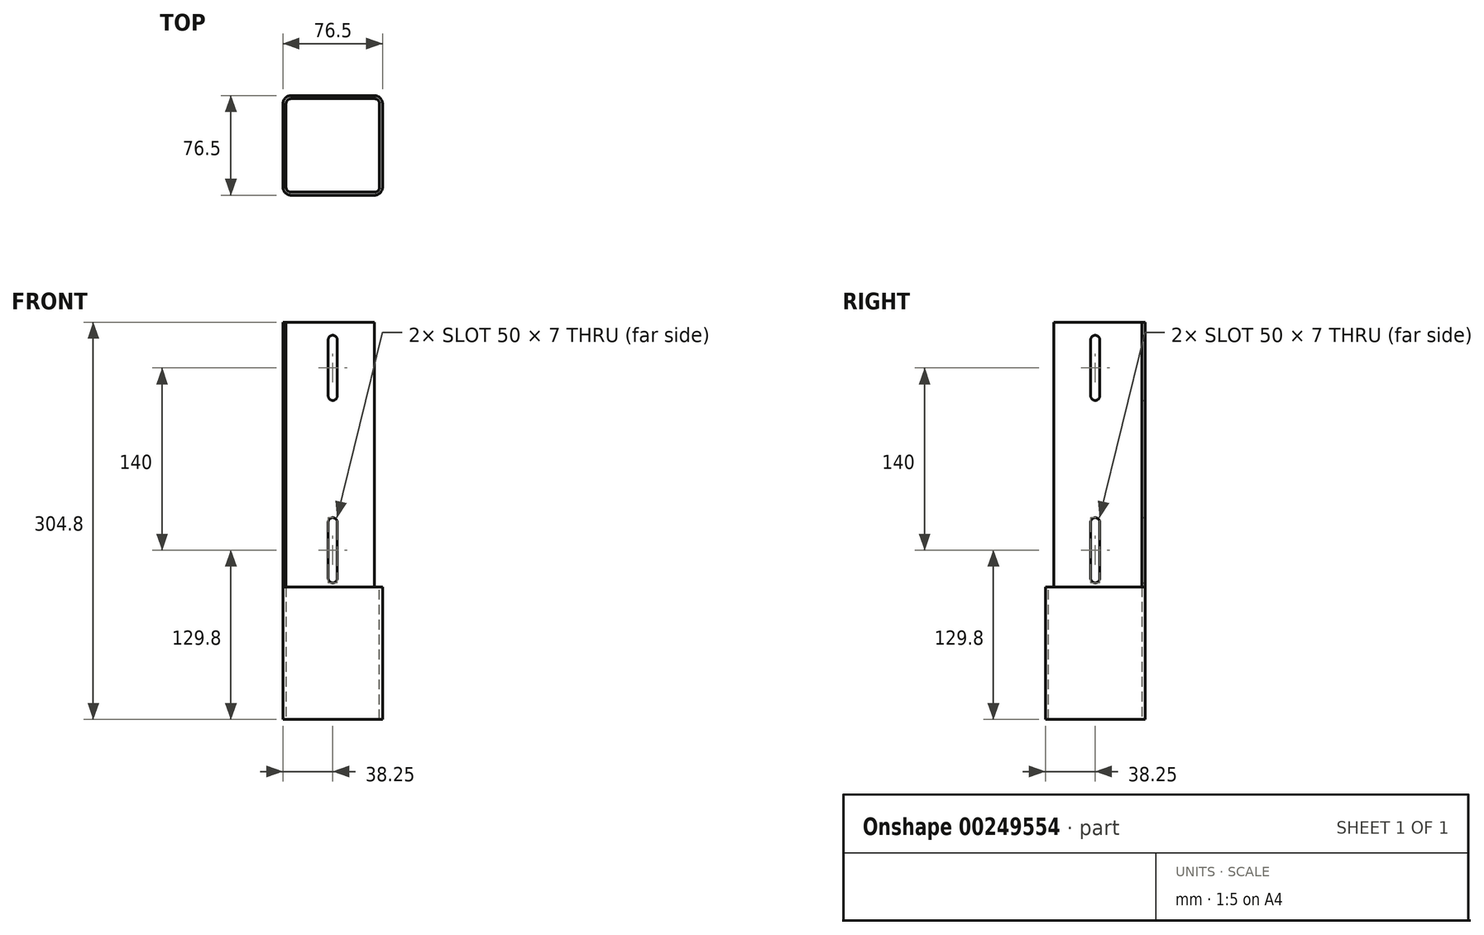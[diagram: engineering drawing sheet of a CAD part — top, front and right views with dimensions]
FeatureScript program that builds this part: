
annotation { "Feature Type Name" : "Feature", "Feature Type Description" : "" }
export const myFeature = defineFeature(function(context is Context, id is Id, definition is map)
    precondition{}
    {
        {
            var Q0;
            Q0=qCreatedBy(makeId("Top.planeOp"),FACE);
            var sketch = newSketch(context, id + "F0", { "sketchPlane" : qUnion([Q0])});
            skLineSegment(sketch, "E0.bottom", {"start": v(31.9, -38.25) * mm, "end": v(-31.9, -38.25) * mm});
            skLineSegment(sketch, "E0.top", {"start": v(31.9, 38.25) * mm, "end": v(-31.9, 38.25) * mm});
            skLineSegment(sketch, "E0.left", {"start": v(38.25, -31.9) * mm, "end": v(38.25, 31.9) * mm});
            skLineSegment(sketch, "E0.right", {"start": v(-38.25, -31.9) * mm, "end": v(-38.25, 31.9) * mm});
            skPoint(sketch, "E0.middle", {"position": v(0, 0) * mm});
            skPoint(sketch, "E1.visualSharp", {"position": v(-38.25, 38.25) * mm});
            skArc(sketch, "E1.filletArc", {"start": v(-31.9, 38.25) * mm, "mid": v(-36.39, 36.39) * mm, "end": v(-38.25, 31.9) * mm});
            skPoint(sketch, "E2.visualSharp", {"position": v(38.25, 38.25) * mm});
            skArc(sketch, "E2.filletArc", {"start": v(38.25, 31.9) * mm, "mid": v(36.39, 36.39) * mm, "end": v(31.9, 38.25) * mm});
            skPoint(sketch, "E3.visualSharp", {"position": v(38.25, -38.25) * mm});
            skArc(sketch, "E3.filletArc", {"start": v(31.9, -38.25) * mm, "mid": v(36.39, -36.39) * mm, "end": v(38.25, -31.9) * mm});
            skPoint(sketch, "E4.visualSharp", {"position": v(-38.25, -38.25) * mm});
            skArc(sketch, "E4.filletArc", {"start": v(-38.25, -31.9) * mm, "mid": v(-36.39, -36.39) * mm, "end": v(-31.9, -38.25) * mm});
            skSolve(sketch);
        }
        {
            var Q0;
            Q0 = qSketchRegion(id + "F0", true);
            extrude(context, id + "F1", {"entities" : qUnion([Q0]), "depth" : 304.8 * mm});
        }
        {
            var Q0;
            Q0=makeQuery(id+"F1.opExtrude","CAP_FACE",FACE,{"disambiguationData":[OSD([sQuery(id+"F0.wireOp",EDGE,"E0.bottom"),sQuery(id+"F0.wireOp",EDGE,"E0.top"),sQuery(id+"F0.wireOp",EDGE,"E0.left"),sQuery(id+"F0.wireOp",EDGE,"E0.right"),sQuery(id+"F0.wireOp",EDGE,"E1.filletArc"),sQuery(id+"F0.wireOp",EDGE,"E2.filletArc"),sQuery(id+"F0.wireOp",EDGE,"E3.filletArc"),sQuery(id+"F0.wireOp",EDGE,"E4.filletArc")])],"isStart":false});
            var Q1;
            Q1=makeQuery(id+"F1.opExtrude","CAP_FACE",FACE,{"disambiguationData":[OSD([sQuery(id+"F0.wireOp",EDGE,"E0.bottom"),sQuery(id+"F0.wireOp",EDGE,"E0.top"),sQuery(id+"F0.wireOp",EDGE,"E0.left"),sQuery(id+"F0.wireOp",EDGE,"E0.right"),sQuery(id+"F0.wireOp",EDGE,"E1.filletArc"),sQuery(id+"F0.wireOp",EDGE,"E2.filletArc"),sQuery(id+"F0.wireOp",EDGE,"E3.filletArc"),sQuery(id+"F0.wireOp",EDGE,"E4.filletArc")])],"isStart":true});
            shell(context, id + "F2", {"entities" : qUnion([Q0, Q1]), "thickness" : 2.36 * mm});
        }
        {
            var Q0;
            Q0=makeQuery(id+"F1.opExtrude","CAP_FACE",FACE,{"disambiguationData":[OSD([sQuery(id+"F0.wireOp",EDGE,"E0.bottom"),sQuery(id+"F0.wireOp",EDGE,"E0.top"),sQuery(id+"F0.wireOp",EDGE,"E0.left"),sQuery(id+"F0.wireOp",EDGE,"E0.right"),sQuery(id+"F0.wireOp",EDGE,"E1.filletArc"),sQuery(id+"F0.wireOp",EDGE,"E2.filletArc"),sQuery(id+"F0.wireOp",EDGE,"E3.filletArc"),sQuery(id+"F0.wireOp",EDGE,"E4.filletArc")])],"isStart":false});
            var sketch = newSketch(context, id + "F3", { "sketchPlane" : qUnion([Q0])});
            skLineSegment(sketch, "E5", {"start": v(-38.25, -31.9) * mm, "end": v(-35.89, -31.9) * mm});
            skLineSegment(sketch, "E6", {"start": v(-35.89, -31.9) * mm, "end": v(31.9, 35.89) * mm});
            skLineSegment(sketch, "E7", {"start": v(31.9, 35.89) * mm, "end": v(31.9, 38.25) * mm});
            skLineSegment(sketch, "E8", {"start": v(31.9, 38.25) * mm, "end": v(63.65, 38.25) * mm});
            skLineSegment(sketch, "E9", {"start": v(63.65, 38.25) * mm, "end": v(63.65, -60.5) * mm});
            skLineSegment(sketch, "E10", {"start": v(-38.25, -31.9) * mm, "end": v(-38.25, -60.5) * mm});
            skLineSegment(sketch, "E11", {"start": v(-38.25, -60.5) * mm, "end": v(63.65, -60.5) * mm});
            skSolve(sketch);
        }
        {
            var Q0;
            Q0 = qSketchRegion(id + "F3", true);
            extrude(context, id + "F4", {"entities" : qUnion([Q0]), "operationType" : NewBodyOperationType.REMOVE, "oppositeDirection" : true, "depth" : 203.2 * mm});
        }
        {
            var Q0;
            Q0=makeQuery(id+"F1.opExtrude","SWEPT_FACE",FACE,{"disambiguationData":[OSD([sQuery(id+"F0.wireOp",EDGE,"E0.right")])]});
            var sketch = newSketch(context, id + "F5", { "sketchPlane" : qUnion([Q0])});
            skLineSegment(sketch, "E12", {"start": v(0, 269.8) * mm, "end": v(0, 129.8) * mm, "construction": true});
            skLineSegment(sketch, "E13.left", {"start": v(3.5, 248.3) * mm, "end": v(3.5, 291.3) * mm});
            skLineSegment(sketch, "E13.right", {"start": v(-3.5, 248.3) * mm, "end": v(-3.5, 291.3) * mm});
            skPoint(sketch, "E13.middle", {"position": v(0, 269.8) * mm});
            skLineSegment(sketch, "E14.left", {"start": v(3.5, 108.3) * mm, "end": v(3.5, 151.3) * mm});
            skLineSegment(sketch, "E14.right", {"start": v(-3.5, 108.3) * mm, "end": v(-3.5, 151.3) * mm});
            skPoint(sketch, "E14.middle", {"position": v(0, 129.8) * mm});
            skArc(sketch, "E15", {"start": v(-3.5, 291.3) * mm, "mid": v(0, 294.8) * mm, "end": v(3.5, 291.3) * mm});
            skArc(sketch, "E16", {"start": v(3.5, 248.3) * mm, "mid": v(0, 244.8) * mm, "end": v(-3.5, 248.3) * mm});
            skArc(sketch, "E17", {"start": v(-3.5, 108.3) * mm, "mid": v(0, 104.8) * mm, "end": v(3.5, 108.3) * mm});
            skArc(sketch, "E18", {"start": v(-3.5, 151.3) * mm, "mid": v(0, 154.8) * mm, "end": v(3.5, 151.3) * mm});
            skSolve(sketch);
        }
        {
            var Q0;
            Q0 = qSketchRegion(id + "F5", true);
            extrude(context, id + "F6", {"entities" : qUnion([Q0]), "operationType" : NewBodyOperationType.REMOVE, "endBound" : BoundingType.THROUGH_ALL, "oppositeDirection" : true, "depth" : 25.4 * mm});
        }
        {
            var Q0;
            Q0=makeQuery(id+"F1.opExtrude","SWEPT_FACE",FACE,{"disambiguationData":[OSD([sQuery(id+"F0.wireOp",EDGE,"E0.top")])]});
            var sketch = newSketch(context, id + "F7", { "sketchPlane" : qUnion([Q0])});
            skLineSegment(sketch, "E19", {"start": v(0, 269.8) * mm, "end": v(0, 129.8) * mm, "construction": true});
            skPoint(sketch, "E19.startSnap0", {"position": v(0, 304.8) * mm});
            skLineSegment(sketch, "E20.left", {"start": v(3.5, 248.3) * mm, "end": v(3.5, 291.3) * mm});
            skLineSegment(sketch, "E20.right", {"start": v(-3.5, 248.3) * mm, "end": v(-3.5, 291.3) * mm});
            skPoint(sketch, "E20.middle", {"position": v(0, 269.8) * mm});
            skLineSegment(sketch, "E21.left", {"start": v(3.5, 108.3) * mm, "end": v(3.5, 151.3) * mm});
            skLineSegment(sketch, "E21.right", {"start": v(-3.5, 108.3) * mm, "end": v(-3.5, 151.3) * mm});
            skPoint(sketch, "E21.middle", {"position": v(0, 129.8) * mm});
            skArc(sketch, "E22", {"start": v(-3.5, 108.3) * mm, "mid": v(0, 104.8) * mm, "end": v(3.5, 108.3) * mm});
            skArc(sketch, "E23", {"start": v(3.5, 151.3) * mm, "mid": v(0, 154.8) * mm, "end": v(-3.5, 151.3) * mm});
            skArc(sketch, "E24", {"start": v(-3.5, 248.3) * mm, "mid": v(0, 244.8) * mm, "end": v(3.5, 248.3) * mm});
            skArc(sketch, "E25", {"start": v(3.5, 291.3) * mm, "mid": v(0, 294.8) * mm, "end": v(-3.5, 291.3) * mm});
            skSolve(sketch);
        }
        {
            var Q0;
            Q0 = qSketchRegion(id + "F7", true);
            extrude(context, id + "F8", {"entities" : qUnion([Q0]), "operationType" : NewBodyOperationType.REMOVE, "endBound" : BoundingType.THROUGH_ALL, "oppositeDirection" : true, "depth" : 25.4 * mm});
        }
    });
